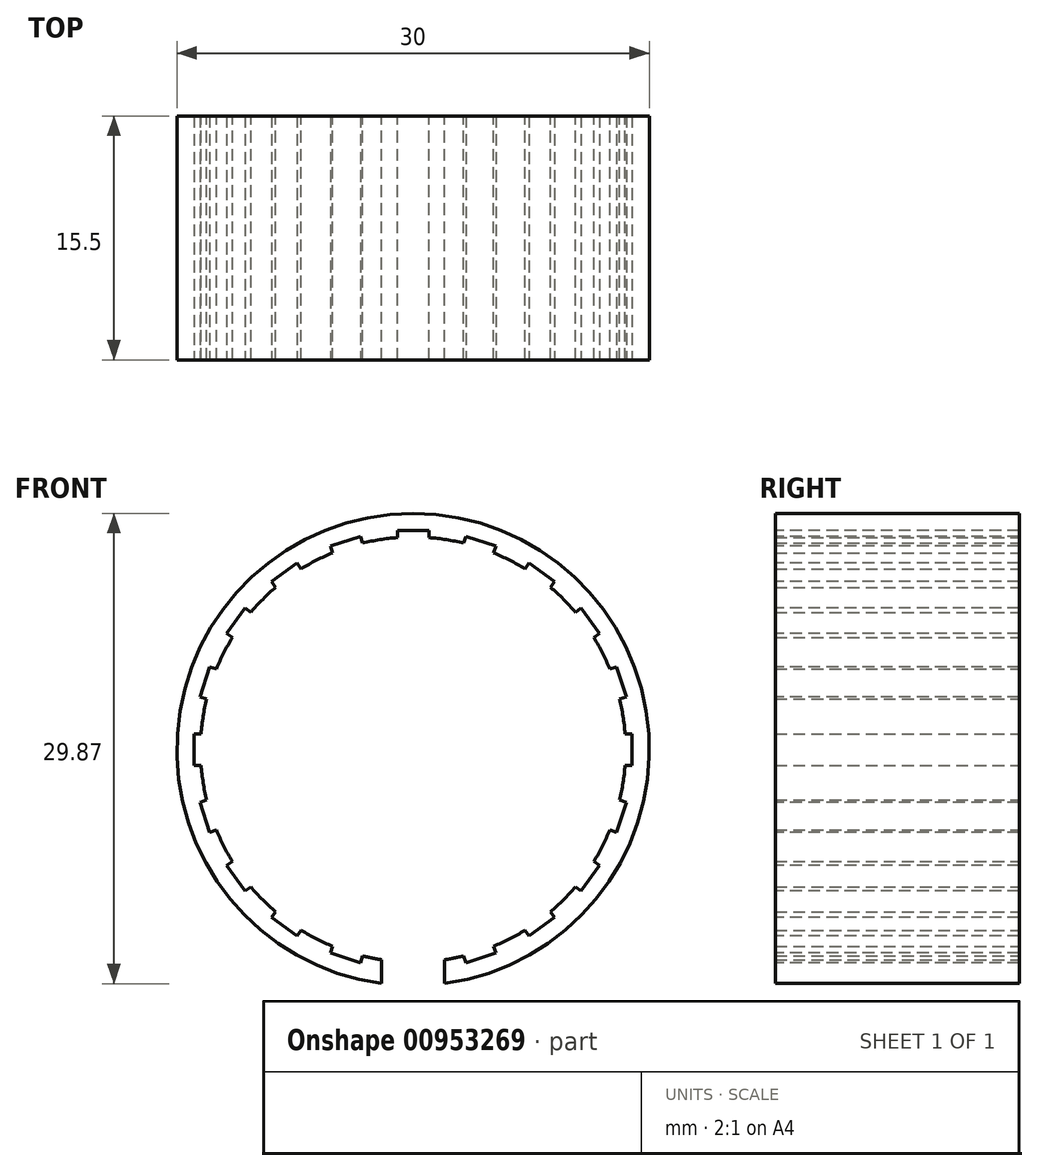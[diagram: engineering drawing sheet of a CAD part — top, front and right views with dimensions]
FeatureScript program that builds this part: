
annotation { "Feature Type Name" : "Feature", "Feature Type Description" : "" }
export const myFeature = defineFeature(function(context is Context, id is Id, definition is map)
    precondition{}
    {
        {
            var Q0;
            Q0=qCreatedBy(makeId("Front.planeOp"),FACE);
            var sketch = newSketch(context, id + "F0", { "sketchPlane" : qUnion([Q0])});
            skCircle(sketch, "E0", {"center": v(0, 0) * mm, "radius": 13.5 * mm});
            skCircle(sketch, "E1", {"center": v(0, 0) * mm, "radius": 15 * mm});
            skSolve(sketch);
        }
        {
            var Q0;
            Q0 = qSketchRegion(id + "F0", true);
            extrude(context, id + "F1", {"entities" : qUnion([Q0]), "depth" : 15.5 * mm, "offsetDistance" : 25 * mm});
        }
        {
            var Q0;
            Q0=qCreatedBy(makeId("Top.planeOp"),FACE);
            var sketch = newSketch(context, id + "F2", { "sketchPlane" : qUnion([Q0])});
            skLineSegment(sketch, "E2.bottom", {"start": v(-2, 1.48) * mm, "end": v(2, 1.48) * mm});
            skLineSegment(sketch, "E2.top", {"start": v(-2, -17.61) * mm, "end": v(2, -17.61) * mm});
            skLineSegment(sketch, "E2.left", {"start": v(-2, 1.48) * mm, "end": v(-2, -17.61) * mm});
            skLineSegment(sketch, "E2.right", {"start": v(2, 1.48) * mm, "end": v(2, -17.61) * mm});
            skSolve(sketch);
        }
        {
            var Q0;
            Q0=makeQuery(id+"F2.imprint","IMPRINT",FACE,{"disambiguationData":[TD([[makeQuery(id+"F2.imprint","IMPRINT",EDGE,{"derivedFrom":sQuery(id+"F2.wireOp",EDGE,"E2.bottom")}),-1.0]])]});
            extrude(context, id + "F3", {"entities" : qUnion([Q0]), "operationType" : NewBodyOperationType.REMOVE, "oppositeDirection" : true, "depth" : 25 * mm, "offsetDistance" : 25 * mm});
        }
        {
            var Q0;
            Q0=qCreatedBy(makeId("Front.planeOp"),FACE);
            var sketch = newSketch(context, id + "F4", { "sketchPlane" : qUnion([Q0])});
            skLineSegment(sketch, "E3.bottom", {"start": v(-1, 13.42) * mm, "end": v(1, 13.42) * mm});
            skLineSegment(sketch, "E3.top", {"start": v(-1, 13.92) * mm, "end": v(1, 13.92) * mm});
            skLineSegment(sketch, "E3.left", {"start": v(-1, 13.42) * mm, "end": v(-1, 13.92) * mm});
            skLineSegment(sketch, "E3.right", {"start": v(1, 13.42) * mm, "end": v(1, 13.92) * mm});
            skLineSegment(sketch, "E4.1.0", {"start": v(-5.1, 12.45) * mm, "end": v(-5.25, 12.93) * mm});
            skLineSegment(sketch, "E4.1.1", {"start": v(-5.25, 12.93) * mm, "end": v(-3.35, 13.54) * mm});
            skLineSegment(sketch, "E4.1.2", {"start": v(-3.2, 13.07) * mm, "end": v(-3.35, 13.54) * mm});
            skLineSegment(sketch, "E4.1.3", {"start": v(-5.1, 12.45) * mm, "end": v(-3.2, 13.07) * mm});
            skLineSegment(sketch, "E4.2.0", {"start": v(-8.7, 10.27) * mm, "end": v(-8.99, 10.67) * mm});
            skLineSegment(sketch, "E4.2.1", {"start": v(-8.99, 10.67) * mm, "end": v(-7.37, 11.85) * mm});
            skLineSegment(sketch, "E4.2.2", {"start": v(-7.08, 11.44) * mm, "end": v(-7.37, 11.85) * mm});
            skLineSegment(sketch, "E4.2.3", {"start": v(-8.7, 10.27) * mm, "end": v(-7.08, 11.44) * mm});
            skLineSegment(sketch, "E4.3.0", {"start": v(-11.44, 7.08) * mm, "end": v(-11.85, 7.37) * mm});
            skLineSegment(sketch, "E4.3.1", {"start": v(-11.85, 7.37) * mm, "end": v(-10.67, 8.99) * mm});
            skLineSegment(sketch, "E4.3.2", {"start": v(-10.27, 8.7) * mm, "end": v(-10.67, 8.99) * mm});
            skLineSegment(sketch, "E4.3.3", {"start": v(-11.44, 7.08) * mm, "end": v(-10.27, 8.7) * mm});
            skLineSegment(sketch, "E4.4.0", {"start": v(-13.07, 3.2) * mm, "end": v(-13.54, 3.35) * mm});
            skLineSegment(sketch, "E4.4.1", {"start": v(-13.54, 3.35) * mm, "end": v(-12.93, 5.25) * mm});
            skLineSegment(sketch, "E4.4.2", {"start": v(-12.45, 5.1) * mm, "end": v(-12.93, 5.25) * mm});
            skLineSegment(sketch, "E4.4.3", {"start": v(-13.07, 3.2) * mm, "end": v(-12.45, 5.1) * mm});
            skLineSegment(sketch, "E4.5.0", {"start": v(-13.42, -1) * mm, "end": v(-13.92, -1) * mm});
            skLineSegment(sketch, "E4.5.1", {"start": v(-13.92, -1) * mm, "end": v(-13.92, 1) * mm});
            skLineSegment(sketch, "E4.5.2", {"start": v(-13.42, 1) * mm, "end": v(-13.92, 1) * mm});
            skLineSegment(sketch, "E4.5.3", {"start": v(-13.42, -1) * mm, "end": v(-13.42, 1) * mm});
            skLineSegment(sketch, "E4.6.0", {"start": v(-12.45, -5.1) * mm, "end": v(-12.93, -5.25) * mm});
            skLineSegment(sketch, "E4.6.1", {"start": v(-12.93, -5.25) * mm, "end": v(-13.54, -3.35) * mm});
            skLineSegment(sketch, "E4.6.2", {"start": v(-13.07, -3.2) * mm, "end": v(-13.54, -3.35) * mm});
            skLineSegment(sketch, "E4.6.3", {"start": v(-12.45, -5.1) * mm, "end": v(-13.07, -3.2) * mm});
            skLineSegment(sketch, "E4.7.0", {"start": v(-10.27, -8.7) * mm, "end": v(-10.67, -8.99) * mm});
            skLineSegment(sketch, "E4.7.1", {"start": v(-10.67, -8.99) * mm, "end": v(-11.85, -7.37) * mm});
            skLineSegment(sketch, "E4.7.2", {"start": v(-11.44, -7.08) * mm, "end": v(-11.85, -7.37) * mm});
            skLineSegment(sketch, "E4.7.3", {"start": v(-10.27, -8.7) * mm, "end": v(-11.44, -7.08) * mm});
            skLineSegment(sketch, "E4.8.0", {"start": v(-7.08, -11.44) * mm, "end": v(-7.37, -11.85) * mm});
            skLineSegment(sketch, "E4.8.1", {"start": v(-7.37, -11.85) * mm, "end": v(-8.99, -10.67) * mm});
            skLineSegment(sketch, "E4.8.2", {"start": v(-8.7, -10.27) * mm, "end": v(-8.99, -10.67) * mm});
            skLineSegment(sketch, "E4.8.3", {"start": v(-7.08, -11.44) * mm, "end": v(-8.7, -10.27) * mm});
            skLineSegment(sketch, "E4.9.0", {"start": v(-3.2, -13.07) * mm, "end": v(-3.35, -13.54) * mm});
            skLineSegment(sketch, "E4.9.1", {"start": v(-3.35, -13.54) * mm, "end": v(-5.25, -12.93) * mm});
            skLineSegment(sketch, "E4.9.2", {"start": v(-5.1, -12.45) * mm, "end": v(-5.25, -12.93) * mm});
            skLineSegment(sketch, "E4.9.3", {"start": v(-3.2, -13.07) * mm, "end": v(-5.1, -12.45) * mm});
            skLineSegment(sketch, "E4.10.0", {"start": v(1, -13.42) * mm, "end": v(1, -13.92) * mm});
            skLineSegment(sketch, "E4.10.1", {"start": v(1, -13.92) * mm, "end": v(-1, -13.92) * mm});
            skLineSegment(sketch, "E4.10.2", {"start": v(-1, -13.42) * mm, "end": v(-1, -13.92) * mm});
            skLineSegment(sketch, "E4.10.3", {"start": v(1, -13.42) * mm, "end": v(-1, -13.42) * mm});
            skLineSegment(sketch, "E4.11.0", {"start": v(5.1, -12.45) * mm, "end": v(5.25, -12.93) * mm});
            skLineSegment(sketch, "E4.11.1", {"start": v(5.25, -12.93) * mm, "end": v(3.35, -13.54) * mm});
            skLineSegment(sketch, "E4.11.2", {"start": v(3.2, -13.07) * mm, "end": v(3.35, -13.54) * mm});
            skLineSegment(sketch, "E4.11.3", {"start": v(5.1, -12.45) * mm, "end": v(3.2, -13.07) * mm});
            skLineSegment(sketch, "E4.12.0", {"start": v(8.7, -10.27) * mm, "end": v(8.99, -10.67) * mm});
            skLineSegment(sketch, "E4.12.1", {"start": v(8.99, -10.67) * mm, "end": v(7.37, -11.85) * mm});
            skLineSegment(sketch, "E4.12.2", {"start": v(7.08, -11.44) * mm, "end": v(7.37, -11.85) * mm});
            skLineSegment(sketch, "E4.12.3", {"start": v(8.7, -10.27) * mm, "end": v(7.08, -11.44) * mm});
            skLineSegment(sketch, "E4.13.0", {"start": v(11.44, -7.08) * mm, "end": v(11.85, -7.37) * mm});
            skLineSegment(sketch, "E4.13.1", {"start": v(11.85, -7.37) * mm, "end": v(10.67, -8.99) * mm});
            skLineSegment(sketch, "E4.13.2", {"start": v(10.27, -8.7) * mm, "end": v(10.67, -8.99) * mm});
            skLineSegment(sketch, "E4.13.3", {"start": v(11.44, -7.08) * mm, "end": v(10.27, -8.7) * mm});
            skLineSegment(sketch, "E4.14.0", {"start": v(13.07, -3.2) * mm, "end": v(13.54, -3.35) * mm});
            skLineSegment(sketch, "E4.14.1", {"start": v(13.54, -3.35) * mm, "end": v(12.93, -5.25) * mm});
            skLineSegment(sketch, "E4.14.2", {"start": v(12.45, -5.1) * mm, "end": v(12.93, -5.25) * mm});
            skLineSegment(sketch, "E4.14.3", {"start": v(13.07, -3.2) * mm, "end": v(12.45, -5.1) * mm});
            skLineSegment(sketch, "E4.15.0", {"start": v(13.42, 1) * mm, "end": v(13.92, 1) * mm});
            skLineSegment(sketch, "E4.15.1", {"start": v(13.92, 1) * mm, "end": v(13.92, -1) * mm});
            skLineSegment(sketch, "E4.15.2", {"start": v(13.42, -1) * mm, "end": v(13.92, -1) * mm});
            skLineSegment(sketch, "E4.15.3", {"start": v(13.42, 1) * mm, "end": v(13.42, -1) * mm});
            skLineSegment(sketch, "E4.16.0", {"start": v(12.45, 5.1) * mm, "end": v(12.93, 5.25) * mm});
            skLineSegment(sketch, "E4.16.1", {"start": v(12.93, 5.25) * mm, "end": v(13.54, 3.35) * mm});
            skLineSegment(sketch, "E4.16.2", {"start": v(13.07, 3.2) * mm, "end": v(13.54, 3.35) * mm});
            skLineSegment(sketch, "E4.16.3", {"start": v(12.45, 5.1) * mm, "end": v(13.07, 3.2) * mm});
            skLineSegment(sketch, "E4.17.0", {"start": v(10.27, 8.7) * mm, "end": v(10.67, 8.99) * mm});
            skLineSegment(sketch, "E4.17.1", {"start": v(10.67, 8.99) * mm, "end": v(11.85, 7.37) * mm});
            skLineSegment(sketch, "E4.17.2", {"start": v(11.44, 7.08) * mm, "end": v(11.85, 7.37) * mm});
            skLineSegment(sketch, "E4.17.3", {"start": v(10.27, 8.7) * mm, "end": v(11.44, 7.08) * mm});
            skLineSegment(sketch, "E4.18.0", {"start": v(7.08, 11.44) * mm, "end": v(7.37, 11.85) * mm});
            skLineSegment(sketch, "E4.18.1", {"start": v(7.37, 11.85) * mm, "end": v(8.99, 10.67) * mm});
            skLineSegment(sketch, "E4.18.2", {"start": v(8.7, 10.27) * mm, "end": v(8.99, 10.67) * mm});
            skLineSegment(sketch, "E4.18.3", {"start": v(7.08, 11.44) * mm, "end": v(8.7, 10.27) * mm});
            skLineSegment(sketch, "E4.19.0", {"start": v(3.2, 13.07) * mm, "end": v(3.35, 13.54) * mm});
            skLineSegment(sketch, "E4.19.1", {"start": v(3.35, 13.54) * mm, "end": v(5.25, 12.93) * mm});
            skLineSegment(sketch, "E4.19.2", {"start": v(5.1, 12.45) * mm, "end": v(5.25, 12.93) * mm});
            skLineSegment(sketch, "E4.19.3", {"start": v(3.2, 13.07) * mm, "end": v(5.1, 12.45) * mm});
            skPoint(sketch, "E4.center", {"position": v(0, 0) * mm});
            skSolve(sketch);
        }
        {
            var Q0;
            Q0 = qSketchRegion(id + "F4", true);
            extrude(context, id + "F5", {"entities" : qUnion([Q0]), "operationType" : NewBodyOperationType.REMOVE, "endBound" : BoundingType.SYMMETRIC, "oppositeDirection" : true, "depth" : 50 * mm, "offsetDistance" : 25 * mm});
        }
    });
